# Revit family: ROBUST-xxx-8xx-Bx
name_source: partatom
category: Leuchten
revit_build: Autodesk Revit 2017 (Build: 20190508_0315(x64)
units: mm (PartAtom-declared; Revit-internal decimal feet)

## family parameters
Basisbauteil = Fläche
Beim Laden mit Abzugskörper schneiden = Nein
Bemaßung runder Anschluss = Durchmesser verwenden
Gemeinsam genutzt = Nein
Lichtquelle = Ja
OmniClass-Nummer = 23.80.70.11
OmniClass-Titel = Luminaries for Internal Lighting
Raumberechnungspunkt = Nein
Teiletyp = Normal

## types (8) — shared parameters
Baugruppenkennzeichen = D5020200
Datei für fotometrisches Netz = ROBUST 15000-840 B.IES
Emissionsform beim Rendern sichtbar = Nein
Farbfilter = 16777215
Farbtemperaturverschiebung bei Dämpfen der Lampe = <Keine Auswahl>
Hersteller = RIDI Leuchten GmbH
Lampe = LED
Neigungswinkel = 90.00°
URL = www.ridi.de
Von Breite des Rechtecks ausssenden = 293 mm
Von Länge des Rechtecks aussenden = 386 mm  [stored 1.2664 ft]
brand = RIDI
conformity mark = CE
electrical safety class = 1
height = 92 mm  [stored 0.301837 ft]
ingress protection (IP) code = IP66
length = 425 mm  [stored 1.39436 ft]
nominal frequency = 50-60Hz
nominal voltage = 230
rated input power = 113
voltage type (AC, DC, UC) = AC
weight = 8.8 kg
width = 414 mm  [stored 1.35827 ft]
zero-valued in all types: Vorgabe-Ansicht

## per-type parameters (varying)
| type | Modell | Scheinlast |
| ROBUST 15000-840 B | 0650575 | 113 VA |
| ROBUST 15000-840 B-DA | 0660575 | 113 VA |
| ROBUST 15000-865 B | 0650639 | 113 VA |
| ROBUST 15000-865 B-DA | 0660639 | 113 VA |
| ROBUST 23000-840 B | 0650576 | 170 VA |
| ROBUST 23000-840 B-DA | 0660576 | 170 VA |
| ROBUST 23000-865 B | 0650634 | 170 VA |
| ROBUST 23000-865 B-DA | 0660634 | 170 VA |

note: column(s) folded — value = type name in every type: product name

note: [stored X ft] marks values corroborated as IEEE doubles in the binary element streams (Revit-internal decimal feet)
